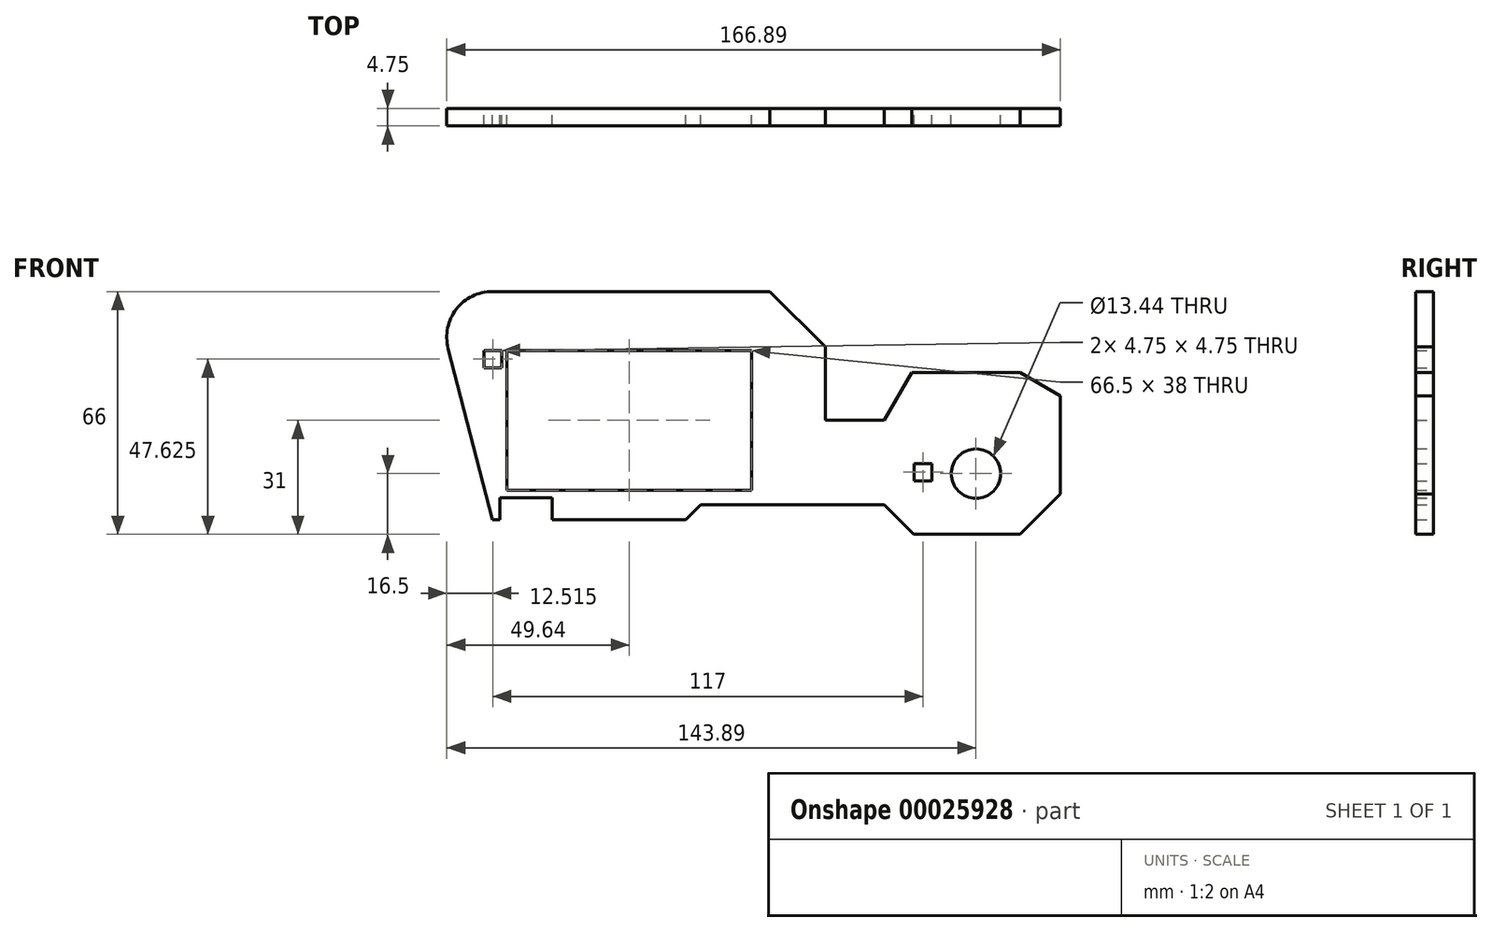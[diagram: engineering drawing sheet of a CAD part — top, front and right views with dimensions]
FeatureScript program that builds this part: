
annotation { "Feature Type Name" : "Feature", "Feature Type Description" : "" }
export const myFeature = defineFeature(function(context is Context, id is Id, definition is map)
    precondition{}
    {
        {
            var Q0;
            Q0=qCreatedBy(makeId("Front.planeOp"),FACE);
            var sketch = newSketch(context, id + "F0", { "sketchPlane" : qUnion([Q0])});
            skLineSegment(sketch, "E0.bottom", {"start": v(0, 0) * mm, "end": v(66.5, 0) * mm});
            skLineSegment(sketch, "E0.top", {"start": v(0, 38) * mm, "end": v(66.5, 38) * mm});
            skLineSegment(sketch, "E0.left", {"start": v(0, 0) * mm, "end": v(0, 38) * mm});
            skLineSegment(sketch, "E0.right", {"start": v(66.5, 0) * mm, "end": v(66.5, 38) * mm});
            skLineSegment(sketch, "E1", {"start": v(-4, -8) * mm, "end": v(-2, -8) * mm});
            skLineSegment(sketch, "E2", {"start": v(48.64, -8) * mm, "end": v(52.64, -4) * mm});
            skLineSegment(sketch, "E3", {"start": v(52.64, -4) * mm, "end": v(102.5, -4) * mm});
            skLineSegment(sketch, "E4", {"start": v(102.5, -4) * mm, "end": v(110.5, -12) * mm});
            skLineSegment(sketch, "E5", {"start": v(110.5, -12) * mm, "end": v(139.5, -12) * mm});
            skLineSegment(sketch, "E6", {"start": v(139.5, -12) * mm, "end": v(150.5, -1) * mm});
            skLineSegment(sketch, "E7", {"start": v(150.5, 25.65) * mm, "end": v(139.5, 32) * mm});
            skLineSegment(sketch, "E8", {"start": v(110, 32) * mm, "end": v(102.5, 19) * mm});
            skLineSegment(sketch, "E9", {"start": v(102.5, 19) * mm, "end": v(86.5, 19) * mm});
            skLineSegment(sketch, "E10", {"start": v(86.5, 19) * mm, "end": v(86.5, 39) * mm});
            skLineSegment(sketch, "E11", {"start": v(86.5, 39) * mm, "end": v(81.13, 44.37) * mm});
            skLineSegment(sketch, "E12", {"start": v(71.5, 54) * mm, "end": v(-4, 54) * mm});
            skArc(sketch, "E13", {"start": v(-4, 54) * mm, "mid": v(-13.8, 49.2) * mm, "end": v(-16, 38.51) * mm});
            skLineSegment(sketch, "E14", {"start": v(-16, 38.51) * mm, "end": v(-4, -8) * mm});
            skCircle(sketch, "E15", {"center": v(127.5, 4.5) * mm, "radius": 6.72 * mm});
            skLineSegment(sketch, "E16.trimOffspring", {"start": v(150.5, 11.24) * mm, "end": v(150.5, 25.65) * mm});
            skLineSegment(sketch, "E17.trimOffspring", {"start": v(75.04, 50.46) * mm, "end": v(71.5, 54) * mm});
            skPoint(sketch, "E18.end.orphan", {"position": v(127.5, 32) * mm});
            skLineSegment(sketch, "E19", {"start": v(110, 32) * mm, "end": v(139.5, 32) * mm});
            skPoint(sketch, "E20.right.end.orphan", {"position": v(136.5, 6.64) * mm});
            skPoint(sketch, "E21.right.end.orphan", {"position": v(136.5, 1.64) * mm});
            skLineSegment(sketch, "E22", {"start": v(150.5, -1) * mm, "end": v(150.5, 11.24) * mm});
            skLineSegment(sketch, "E23", {"start": v(75.04, 50.46) * mm, "end": v(81.13, 44.37) * mm});
            skLineSegment(sketch, "E24.bottom", {"start": v(-1.5, 38) * mm, "end": v(-6.25, 38) * mm});
            skLineSegment(sketch, "E24.top", {"start": v(-1.5, 33.25) * mm, "end": v(-6.25, 33.25) * mm});
            skLineSegment(sketch, "E24.left", {"start": v(-1.5, 38) * mm, "end": v(-1.5, 33.25) * mm});
            skLineSegment(sketch, "E24.right", {"start": v(-6.25, 38) * mm, "end": v(-6.25, 33.25) * mm});
            skLineSegment(sketch, "E25.bottom", {"start": v(110.75, 7.25) * mm, "end": v(115.5, 7.25) * mm});
            skLineSegment(sketch, "E25.top", {"start": v(110.75, 2.5) * mm, "end": v(115.5, 2.5) * mm});
            skLineSegment(sketch, "E25.left", {"start": v(110.75, 7.25) * mm, "end": v(110.75, 2.5) * mm});
            skLineSegment(sketch, "E25.right", {"start": v(115.5, 7.25) * mm, "end": v(115.5, 2.5) * mm});
            skLineSegment(sketch, "E26", {"start": v(-2, -8) * mm, "end": v(-2, -2) * mm});
            skLineSegment(sketch, "E27", {"start": v(-2, -2) * mm, "end": v(12.25, -2) * mm});
            skLineSegment(sketch, "E28", {"start": v(12.25, -2) * mm, "end": v(12.25, -8) * mm});
            skLineSegment(sketch, "E29.trimOffspring", {"start": v(12.25, -8) * mm, "end": v(48.64, -8) * mm});
            skSolve(sketch);
        }
        {
            var Q0;
            Q0=qSketchRegion(id+"F0",true);
            extrude(context, id + "F1", {"entities" : qUnion([Q0]), "depth" : 4.75 * mm});
        }
    });
